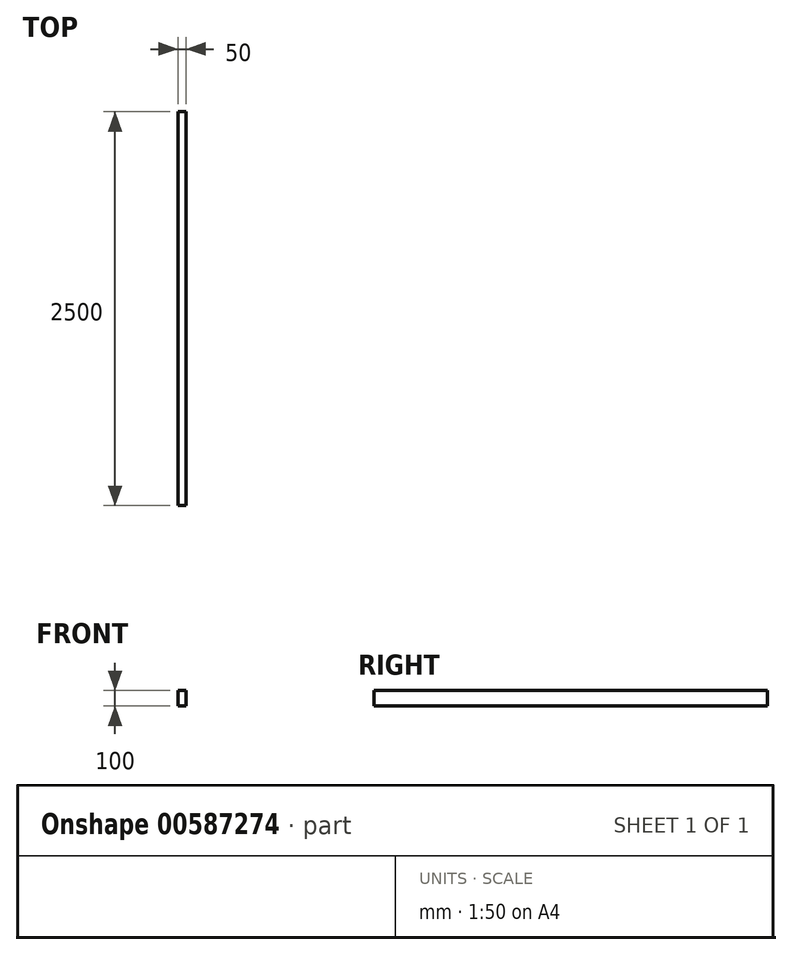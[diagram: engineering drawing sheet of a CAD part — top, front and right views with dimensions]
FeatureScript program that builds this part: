
annotation { "Feature Type Name" : "Feature", "Feature Type Description" : "" }
export const myFeature = defineFeature(function(context is Context, id is Id, definition is map)
    precondition{}
    {
        {
            var Q0;
            Q0=qCreatedBy(makeId("Front.planeOp"),FACE);
            var sketch = newSketch(context, id + "F0", { "sketchPlane" : qUnion([Q0])});
            skLineSegment(sketch, "E0.bottom", {"start": v(25, 50) * mm, "end": v(-25, 50) * mm});
            skLineSegment(sketch, "E0.top", {"start": v(25, -50) * mm, "end": v(-25, -50) * mm});
            skLineSegment(sketch, "E0.left", {"start": v(25, 50) * mm, "end": v(25, -50) * mm});
            skLineSegment(sketch, "E0.right", {"start": v(-25, 50) * mm, "end": v(-25, -50) * mm});
            skPoint(sketch, "E0.middle", {"position": v(0, 0) * mm});
            skSolve(sketch);
        }
        {
            var Q0;
            Q0=makeQuery(id+"F0.imprint","IMPRINT",FACE,{"disambiguationData":[TD([[makeQuery(id+"F0.imprint","IMPRINT",EDGE,{"derivedFrom":sQuery(id+"F0.wireOp",EDGE,"E0.bottom")}),1.0]])]});
            extrude(context, id + "F1", {"entities" : qUnion([Q0]), "endBound" : BoundingType.SYMMETRIC, "depth" : 2500 * mm, "offsetDistance" : 25.4 * mm});
        }
    });
